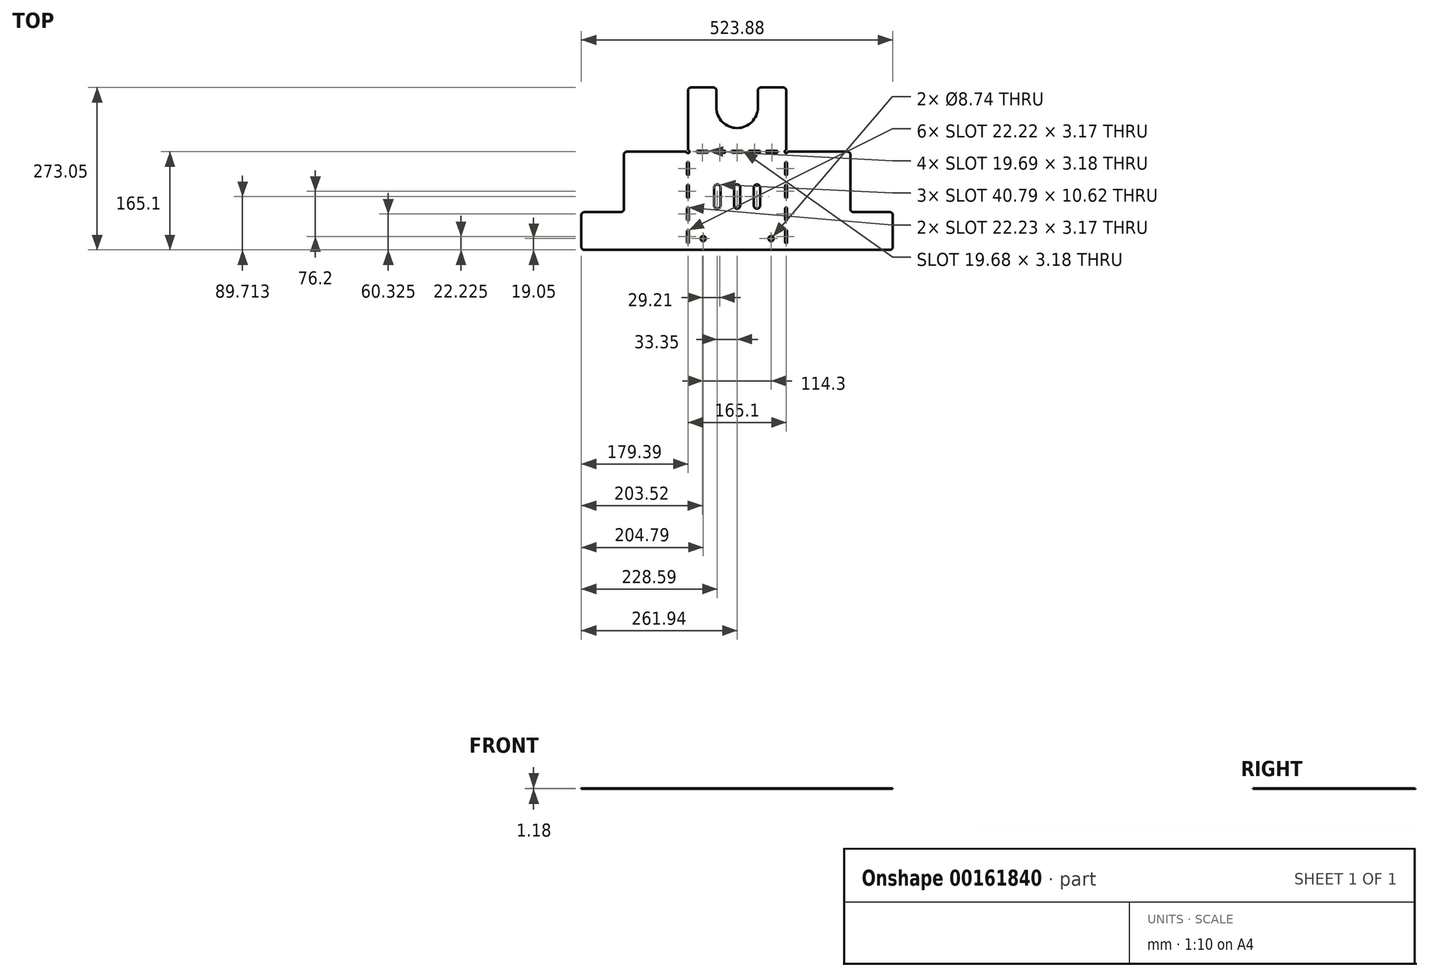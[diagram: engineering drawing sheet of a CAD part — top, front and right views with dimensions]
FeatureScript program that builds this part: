
annotation { "Feature Type Name" : "Feature", "Feature Type Description" : "" }
export const myFeature = defineFeature(function(context is Context, id is Id, definition is map)
    precondition{}
    {
        {
            var Q0;
            Q0=qCreatedBy(makeId("Top.planeOp"),FACE);
            var sketch = newSketch(context, id + "F0", { "sketchPlane" : qUnion([Q0])});
            skLineSegment(sketch, "E0", {"start": v(-82.55, 0) * mm, "end": v(82.55, 0) * mm});
            skLineSegment(sketch, "E1", {"start": v(-82.55, 0) * mm, "end": v(-82.55, 165.1) * mm});
            skLineSegment(sketch, "E2", {"start": v(82.55, 0) * mm, "end": v(82.55, 165.1) * mm});
            skLineSegment(sketch, "E3", {"start": v(-82.55, 165.1) * mm, "end": v(82.55, 165.1) * mm});
            skLineSegment(sketch, "E4", {"start": v(82.55, 0) * mm, "end": v(261.94, 0) * mm});
            skLineSegment(sketch, "E5", {"start": v(261.94, 0) * mm, "end": v(261.94, 63.5) * mm});
            skLineSegment(sketch, "E6", {"start": v(261.94, 63.5) * mm, "end": v(190.5, 63.5) * mm});
            skLineSegment(sketch, "E7", {"start": v(190.5, 63.5) * mm, "end": v(190.5, 165.1) * mm});
            skLineSegment(sketch, "E8", {"start": v(190.5, 165.1) * mm, "end": v(82.55, 165.1) * mm});
            skLineSegment(sketch, "E9", {"start": v(-82.55, 0) * mm, "end": v(-261.94, 0) * mm});
            skLineSegment(sketch, "E10", {"start": v(-261.94, 0) * mm, "end": v(-261.94, 63.5) * mm});
            skLineSegment(sketch, "E11", {"start": v(-261.94, 63.5) * mm, "end": v(-190.5, 63.5) * mm});
            skLineSegment(sketch, "E12", {"start": v(-190.5, 63.5) * mm, "end": v(-190.5, 165.1) * mm});
            skLineSegment(sketch, "E13", {"start": v(-190.5, 165.1) * mm, "end": v(-82.55, 165.1) * mm});
            skLineSegment(sketch, "E14", {"start": v(-82.55, 165.1) * mm, "end": v(-82.55, 273.05) * mm});
            skLineSegment(sketch, "E15", {"start": v(-82.55, 273.05) * mm, "end": v(-34.93, 273.05) * mm});
            skLineSegment(sketch, "E16", {"start": v(82.55, 273.05) * mm, "end": v(82.55, 165.1) * mm});
            skLineSegment(sketch, "E17", {"start": v(0, 0) * mm, "end": v(0, 365.08) * mm, "construction": true});
            skArc(sketch, "E18", {"start": v(-34.93, 239.8) * mm, "mid": v(0, 204.88) * mm, "end": v(34.93, 239.8) * mm});
            skLineSegment(sketch, "E19", {"start": v(-34.93, 239.8) * mm, "end": v(-34.93, 273.05) * mm});
            skLineSegment(sketch, "E20", {"start": v(34.93, 239.8) * mm, "end": v(34.93, 273.05) * mm});
            skLineSegment(sketch, "E21.trimOffspring", {"start": v(34.93, 273.05) * mm, "end": v(82.55, 273.05) * mm});
            skLineSegment(sketch, "E22", {"start": v(-84.14, 165.1) * mm, "end": v(-84.14, 0) * mm});
            skLineSegment(sketch, "E23", {"start": v(84.14, 165.1) * mm, "end": v(84.14, 0) * mm});
            skSolve(sketch);
        }
        {
            var Q0;
            Q0 = qSketchRegion(id + "F0", true);
            extrude(context, id + "F1", {"entities" : qUnion([Q0]), "depth" : 1.18 * mm});
        }
        {
            var Q0;
            Q0=makeQuery(id+"F1.opExtrude","CAP_FACE",FACE,{"disambiguationData":[OSD([sQuery(id+"F0.wireOp",EDGE,"E0"),sQuery(id+"F0.wireOp",EDGE,"E4"),sQuery(id+"F0.wireOp",EDGE,"E5"),sQuery(id+"F0.wireOp",EDGE,"E6"),sQuery(id+"F0.wireOp",EDGE,"E7"),sQuery(id+"F0.wireOp",EDGE,"E8"),sQuery(id+"F0.wireOp",EDGE,"E9"),sQuery(id+"F0.wireOp",EDGE,"E10"),sQuery(id+"F0.wireOp",EDGE,"E11"),sQuery(id+"F0.wireOp",EDGE,"E12"),sQuery(id+"F0.wireOp",EDGE,"E13"),sQuery(id+"F0.wireOp",EDGE,"E14"),sQuery(id+"F0.wireOp",EDGE,"E15"),sQuery(id+"F0.wireOp",EDGE,"E16"),sQuery(id+"F0.wireOp",EDGE,"E18"),sQuery(id+"F0.wireOp",EDGE,"E19"),sQuery(id+"F0.wireOp",EDGE,"E20"),sQuery(id+"F0.wireOp",EDGE,"E21.trimOffspring")])],"isStart":false});
            var sketch = newSketch(context, id + "F2", { "sketchPlane" : qUnion([Q0])});
            skLineSegment(sketch, "E24.0", {"start": v(261.94, 0) * mm, "end": v(-261.94, 0) * mm});
            skPoint(sketch, "E25.0", {"position": v(0, 0) * mm});
            skLineSegment(sketch, "E26", {"start": v(0, 74.63) * mm, "end": v(0, 104.8) * mm, "construction": true});
            skLineSegment(sketch, "E27", {"start": v(-123.7, 19.05) * mm, "end": v(130.02, 19.05) * mm, "construction": true});
            skLineSegment(sketch, "E28", {"start": v(-57.15, 51.44) * mm, "end": v(-57.15, -23.28) * mm, "construction": true});
            skLineSegment(sketch, "E29", {"start": v(57.15, 51.05) * mm, "end": v(57.15, -26) * mm, "construction": true});
            skCircle(sketch, "E30", {"center": v(-57.15, 19.05) * mm, "radius": 4.37 * mm});
            skCircle(sketch, "E31", {"center": v(57.15, 19.05) * mm, "radius": 4.37 * mm});
            skLineSegment(sketch, "E32", {"start": v(-208.63, 104.8) * mm, "end": v(250.8, 104.8) * mm, "construction": true});
            skLineSegment(sketch, "E33", {"start": v(-210.6, 74.63) * mm, "end": v(258, 74.63) * mm, "construction": true});
            skLineSegment(sketch, "E34", {"start": v(-33.35, 104.8) * mm, "end": v(-33.35, 74.63) * mm, "construction": true});
            skLineSegment(sketch, "E35", {"start": v(33.35, 104.8) * mm, "end": v(33.35, 74.63) * mm, "construction": true});
            skArc(sketch, "E36.0.startCap", {"start": v(-38.66, 104.8) * mm, "mid": v(-33.35, 110.1) * mm, "end": v(-28.04, 104.8) * mm});
            skArc(sketch, "E36.0.endCap", {"start": v(-28.04, 74.63) * mm, "mid": v(-33.35, 69.32) * mm, "end": v(-38.66, 74.63) * mm});
            skLineSegment(sketch, "E36.0.left", {"start": v(-28.04, 104.8) * mm, "end": v(-28.04, 74.63) * mm});
            skLineSegment(sketch, "E36.0.right", {"start": v(-38.66, 104.8) * mm, "end": v(-38.66, 74.63) * mm});
            skArc(sketch, "E37.0.startCap", {"start": v(5.3, 74.63) * mm, "mid": v(0, 69.32) * mm, "end": v(-5.3, 74.63) * mm});
            skArc(sketch, "E37.0.endCap", {"start": v(-5.3, 104.8) * mm, "mid": v(0, 110.1) * mm, "end": v(5.3, 104.8) * mm});
            skLineSegment(sketch, "E37.0.left", {"start": v(-5.3, 74.63) * mm, "end": v(-5.3, 104.8) * mm});
            skLineSegment(sketch, "E37.0.right", {"start": v(5.3, 74.63) * mm, "end": v(5.3, 104.8) * mm});
            skArc(sketch, "E38.0.startCap", {"start": v(28.04, 104.8) * mm, "mid": v(33.35, 110.1) * mm, "end": v(38.66, 104.8) * mm});
            skArc(sketch, "E38.0.endCap", {"start": v(38.66, 74.63) * mm, "mid": v(33.35, 69.32) * mm, "end": v(28.04, 74.63) * mm});
            skLineSegment(sketch, "E38.0.left", {"start": v(38.66, 104.8) * mm, "end": v(38.66, 74.63) * mm});
            skLineSegment(sketch, "E38.0.right", {"start": v(28.04, 104.8) * mm, "end": v(28.04, 74.63) * mm});
            skSolve(sketch);
        }
        {
            var Q0;
            Q0 = qSketchRegion(id + "F2", true);
            extrude(context, id + "F3", {"entities" : qUnion([Q0]), "operationType" : NewBodyOperationType.REMOVE, "endBound" : BoundingType.UP_TO_NEXT, "oppositeDirection" : true, "depth" : 25.4 * mm});
        }
        {
            var Q0;
            Q0=makeQuery(id+"F1.opExtrude","SWEPT_EDGE",EDGE,{"disambiguationData":[OSD([sQuery(id+"F0.wireOp",EDGE,"E14"),sQuery(id+"F0.wireOp",EDGE,"E15")])]});
            var Q1;
            Q1=makeQuery(id+"F1.opExtrude","SWEPT_EDGE",EDGE,{"disambiguationData":[OSD([sQuery(id+"F0.wireOp",EDGE,"E15"),sQuery(id+"F0.wireOp",EDGE,"E19")])]});
            var Q2;
            Q2=makeQuery(id+"F1.opExtrude","SWEPT_EDGE",EDGE,{"disambiguationData":[OSD([sQuery(id+"F0.wireOp",EDGE,"E20"),sQuery(id+"F0.wireOp",EDGE,"E21.trimOffspring")])]});
            var Q3;
            Q3=makeQuery(id+"F1.opExtrude","SWEPT_EDGE",EDGE,{"disambiguationData":[OSD([sQuery(id+"F0.wireOp",EDGE,"E16"),sQuery(id+"F0.wireOp",EDGE,"E21.trimOffspring")])]});
            var Q4;
            Q4=makeQuery(id+"F1.opExtrude","SWEPT_EDGE",EDGE,{"disambiguationData":[OSD([sQuery(id+"F0.wireOp",EDGE,"E7"),sQuery(id+"F0.wireOp",EDGE,"E8")])]});
            var Q5;
            Q5=makeQuery(id+"F1.opExtrude","SWEPT_EDGE",EDGE,{"disambiguationData":[OSD([sQuery(id+"F0.wireOp",EDGE,"E5"),sQuery(id+"F0.wireOp",EDGE,"E6")])]});
            var Q6;
            Q6=makeQuery(id+"F1.opExtrude","SWEPT_EDGE",EDGE,{"disambiguationData":[OSD([sQuery(id+"F0.wireOp",EDGE,"E6"),sQuery(id+"F0.wireOp",EDGE,"E7")])]});
            var Q7;
            Q7=makeQuery(id+"F1.opExtrude","SWEPT_EDGE",EDGE,{"disambiguationData":[OSD([sQuery(id+"F0.wireOp",EDGE,"E4"),sQuery(id+"F0.wireOp",EDGE,"E5")])]});
            var Q8;
            Q8=makeQuery(id+"F1.opExtrude","SWEPT_EDGE",EDGE,{"disambiguationData":[OSD([sQuery(id+"F0.wireOp",EDGE,"E9"),sQuery(id+"F0.wireOp",EDGE,"E10")])]});
            var Q9;
            Q9=makeQuery(id+"F1.opExtrude","SWEPT_EDGE",EDGE,{"disambiguationData":[OSD([sQuery(id+"F0.wireOp",EDGE,"E10"),sQuery(id+"F0.wireOp",EDGE,"E11")])]});
            var Q10;
            Q10=makeQuery(id+"F1.opExtrude","SWEPT_EDGE",EDGE,{"disambiguationData":[OSD([sQuery(id+"F0.wireOp",EDGE,"E11"),sQuery(id+"F0.wireOp",EDGE,"E12")])]});
            var Q11;
            Q11=makeQuery(id+"F1.opExtrude","SWEPT_EDGE",EDGE,{"disambiguationData":[OSD([sQuery(id+"F0.wireOp",EDGE,"E12"),sQuery(id+"F0.wireOp",EDGE,"E13")])]});
            fillet(context, id + "F4", {"entities" : qUnion([Q0, Q1, Q2, Q3, Q4, Q5, Q6, Q7, Q8, Q9, Q10, Q11]), "radius" : 5.08 * mm, "tangentPropagation" : true, "allowEdgeOverflow" : false});
        }
        {
            var Q0;
            Q0=makeQuery(id+"F1.opExtrude","CAP_FACE",FACE,{"disambiguationData":[OSD([sQuery(id+"F0.wireOp",EDGE,"E0"),sQuery(id+"F0.wireOp",EDGE,"E4"),sQuery(id+"F0.wireOp",EDGE,"E5"),sQuery(id+"F0.wireOp",EDGE,"E6"),sQuery(id+"F0.wireOp",EDGE,"E7"),sQuery(id+"F0.wireOp",EDGE,"E8"),sQuery(id+"F0.wireOp",EDGE,"E9"),sQuery(id+"F0.wireOp",EDGE,"E10"),sQuery(id+"F0.wireOp",EDGE,"E11"),sQuery(id+"F0.wireOp",EDGE,"E12"),sQuery(id+"F0.wireOp",EDGE,"E13"),sQuery(id+"F0.wireOp",EDGE,"E14"),sQuery(id+"F0.wireOp",EDGE,"E15"),sQuery(id+"F0.wireOp",EDGE,"E16"),sQuery(id+"F0.wireOp",EDGE,"E18"),sQuery(id+"F0.wireOp",EDGE,"E19"),sQuery(id+"F0.wireOp",EDGE,"E20"),sQuery(id+"F0.wireOp",EDGE,"E21.trimOffspring")])],"isStart":false});
            var sketch = newSketch(context, id + "F5", { "sketchPlane" : qUnion([Q0])});
            skLineSegment(sketch, "E39", {"start": v(-82.55, 146.05) * mm, "end": v(-82.55, 127) * mm});
            skLineSegment(sketch, "E40", {"start": v(0, -35.73) * mm, "end": v(0, 222.95) * mm, "construction": true});
            skPoint(sketch, "E41", {"position": v(-82.55, 146.05) * mm});
            skPoint(sketch, "E42.0.1.0", {"position": v(-82.55, 127) * mm});
            skPoint(sketch, "E42.0.2.0", {"position": v(-82.55, 107.95) * mm});
            skPoint(sketch, "E42.0.3.0", {"position": v(-82.55, 88.9) * mm});
            skPoint(sketch, "E42.0.4.0", {"position": v(-82.55, 69.85) * mm});
            skPoint(sketch, "E42.0.5.0", {"position": v(-82.55, 50.8) * mm});
            skPoint(sketch, "E42.0.6.0", {"position": v(-82.55, 31.75) * mm});
            skPoint(sketch, "E42.0.7.0", {"position": v(-82.55, 12.7) * mm});
            skLineSegment(sketch, "E42.direction1", {"start": v(-82.55, 146.05) * mm, "end": v(-57.15, 146.05) * mm, "construction": true});
            skLineSegment(sketch, "E42.direction2", {"start": v(-82.55, 146.05) * mm, "end": v(-82.55, 127) * mm, "construction": true});
            skPoint(sketch, "E43.orphan", {"position": v(-82.55, 165.1) * mm});
            skLineSegment(sketch, "E44.trimOffspring", {"start": v(-82.55, 107.95) * mm, "end": v(-82.55, 88.9) * mm});
            skPoint(sketch, "E45.orphan", {"position": v(-82.55, 0) * mm});
            skLineSegment(sketch, "E46.trimOffspring", {"start": v(-82.55, 31.75) * mm, "end": v(-82.55, 12.7) * mm});
            skLineSegment(sketch, "E47.trimOffspring", {"start": v(-82.55, 69.85) * mm, "end": v(-82.55, 50.8) * mm});
            skArc(sketch, "E48.0.startCap", {"start": v(-84.14, 146.05) * mm, "mid": v(-82.55, 147.64) * mm, "end": v(-80.96, 146.05) * mm});
            skArc(sketch, "E48.0.endCap", {"start": v(-80.96, 127) * mm, "mid": v(-82.55, 125.41) * mm, "end": v(-84.14, 127) * mm});
            skLineSegment(sketch, "E48.0.left", {"start": v(-80.96, 146.05) * mm, "end": v(-80.96, 127) * mm});
            skLineSegment(sketch, "E48.0.right", {"start": v(-84.14, 146.05) * mm, "end": v(-84.14, 127) * mm});
            skArc(sketch, "E48.1.startCap", {"start": v(-84.14, 107.95) * mm, "mid": v(-82.55, 109.54) * mm, "end": v(-80.96, 107.95) * mm});
            skArc(sketch, "E48.1.endCap", {"start": v(-80.96, 88.9) * mm, "mid": v(-82.55, 87.31) * mm, "end": v(-84.14, 88.9) * mm});
            skLineSegment(sketch, "E48.1.left", {"start": v(-80.96, 107.95) * mm, "end": v(-80.96, 88.9) * mm});
            skLineSegment(sketch, "E48.1.right", {"start": v(-84.14, 107.95) * mm, "end": v(-84.14, 88.9) * mm});
            skArc(sketch, "E48.2.startCap", {"start": v(-84.14, 69.85) * mm, "mid": v(-82.55, 71.44) * mm, "end": v(-80.96, 69.85) * mm});
            skArc(sketch, "E48.2.endCap", {"start": v(-80.96, 50.8) * mm, "mid": v(-82.55, 49.21) * mm, "end": v(-84.14, 50.8) * mm});
            skLineSegment(sketch, "E48.2.left", {"start": v(-80.96, 69.85) * mm, "end": v(-80.96, 50.8) * mm});
            skLineSegment(sketch, "E48.2.right", {"start": v(-84.14, 69.85) * mm, "end": v(-84.14, 50.8) * mm});
            skArc(sketch, "E48.3.startCap", {"start": v(-84.14, 31.75) * mm, "mid": v(-82.55, 33.34) * mm, "end": v(-80.96, 31.75) * mm});
            skArc(sketch, "E48.3.endCap", {"start": v(-80.96, 12.7) * mm, "mid": v(-82.55, 11.11) * mm, "end": v(-84.14, 12.7) * mm});
            skLineSegment(sketch, "E48.3.left", {"start": v(-80.96, 31.75) * mm, "end": v(-80.96, 12.7) * mm});
            skLineSegment(sketch, "E48.3.right", {"start": v(-84.14, 31.75) * mm, "end": v(-84.14, 12.7) * mm});
            skArc(sketch, "E49.MirrorCS", {"start": v(84.14, 146.05) * mm, "mid": v(82.55, 147.64) * mm, "end": v(80.96, 146.05) * mm});
            skArc(sketch, "E50.MirrorCS", {"start": v(80.96, 127) * mm, "mid": v(82.55, 125.41) * mm, "end": v(84.14, 127) * mm});
            skArc(sketch, "E51.MirrorCS", {"start": v(80.96, 88.9) * mm, "mid": v(82.55, 87.31) * mm, "end": v(84.14, 88.9) * mm});
            skArc(sketch, "E52.MirrorCS", {"start": v(84.14, 107.95) * mm, "mid": v(82.55, 109.54) * mm, "end": v(80.96, 107.95) * mm});
            skArc(sketch, "E53.MirrorCS", {"start": v(84.14, 69.85) * mm, "mid": v(82.55, 71.44) * mm, "end": v(80.96, 69.85) * mm});
            skArc(sketch, "E54.MirrorCS", {"start": v(80.96, 12.7) * mm, "mid": v(82.55, 11.11) * mm, "end": v(84.14, 12.7) * mm});
            skArc(sketch, "E55.MirrorCS", {"start": v(84.14, 31.75) * mm, "mid": v(82.55, 33.34) * mm, "end": v(80.96, 31.75) * mm});
            skArc(sketch, "E56.MirrorCS", {"start": v(80.96, 50.8) * mm, "mid": v(82.55, 49.21) * mm, "end": v(84.14, 50.8) * mm});
            skLineSegment(sketch, "E57.MirrorCS", {"start": v(82.55, 146.05) * mm, "end": v(82.55, 127) * mm});
            skLineSegment(sketch, "E58.MirrorCS", {"start": v(84.14, 69.85) * mm, "end": v(84.14, 50.8) * mm});
            skLineSegment(sketch, "E59.MirrorCS", {"start": v(84.14, 31.75) * mm, "end": v(84.14, 12.7) * mm});
            skLineSegment(sketch, "E60.MirrorCS", {"start": v(84.14, 146.05) * mm, "end": v(84.14, 127) * mm});
            skLineSegment(sketch, "E61.MirrorCS", {"start": v(80.96, 146.05) * mm, "end": v(80.96, 127) * mm});
            skLineSegment(sketch, "E62.MirrorCS", {"start": v(82.55, 69.85) * mm, "end": v(82.55, 50.8) * mm});
            skLineSegment(sketch, "E63.MirrorCS", {"start": v(82.55, 31.75) * mm, "end": v(82.55, 12.7) * mm});
            skLineSegment(sketch, "E64.MirrorCS", {"start": v(82.55, 107.95) * mm, "end": v(82.55, 88.9) * mm});
            skPoint(sketch, "E65.MirrorP", {"position": v(82.55, 165.1) * mm});
            skLineSegment(sketch, "E66.MirrorCS", {"start": v(82.55, 146.05) * mm, "end": v(82.55, 127) * mm, "construction": true});
            skLineSegment(sketch, "E67.MirrorCS", {"start": v(84.14, 107.95) * mm, "end": v(84.14, 88.9) * mm});
            skLineSegment(sketch, "E68.MirrorCS", {"start": v(80.96, 69.85) * mm, "end": v(80.96, 50.8) * mm});
            skLineSegment(sketch, "E69.MirrorCS", {"start": v(80.96, 31.75) * mm, "end": v(80.96, 12.7) * mm});
            skLineSegment(sketch, "E70.MirrorCS", {"start": v(80.96, 107.95) * mm, "end": v(80.96, 88.9) * mm});
            skLineSegment(sketch, "E71", {"start": v(-66.68, 165.1) * mm, "end": v(-50.17, 165.1) * mm});
            skPoint(sketch, "E72", {"position": v(-66.68, 165.1) * mm});
            skPoint(sketch, "E73", {"position": v(66.68, 165.1) * mm});
            skPoint(sketch, "E74", {"position": v(-37.47, 165.1) * mm});
            skPoint(sketch, "E75", {"position": v(0, 165.1) * mm});
            skPoint(sketch, "E76", {"position": v(37.47, 165.1) * mm});
            skPoint(sketch, "E77", {"position": v(-20.96, 165.1) * mm});
            skPoint(sketch, "E78", {"position": v(20.96, 165.1) * mm});
            skPoint(sketch, "E79", {"position": v(-8.26, 165.1) * mm});
            skPoint(sketch, "E80", {"position": v(8.26, 165.1) * mm});
            skLineSegment(sketch, "E81.trimOffspring", {"start": v(-8.26, 165.1) * mm, "end": v(8.26, 165.1) * mm});
            skLineSegment(sketch, "E82.trimOffspring", {"start": v(20.96, 165.1) * mm, "end": v(37.47, 165.1) * mm});
            skPoint(sketch, "E83", {"position": v(50.17, 165.1) * mm});
            skPoint(sketch, "E84", {"position": v(-50.17, 165.1) * mm});
            skLineSegment(sketch, "E85.trimOffspring", {"start": v(-37.47, 165.1) * mm, "end": v(-20.96, 165.1) * mm});
            skLineSegment(sketch, "E86.trimOffspring", {"start": v(50.17, 165.1) * mm, "end": v(66.68, 165.1) * mm});
            skArc(sketch, "E87.0.startCap", {"start": v(-66.68, 163.51) * mm, "mid": v(-68.26, 165.1) * mm, "end": v(-66.68, 166.69) * mm});
            skArc(sketch, "E87.0.endCap", {"start": v(-50.17, 166.69) * mm, "mid": v(-48.58, 165.1) * mm, "end": v(-50.17, 163.51) * mm});
            skLineSegment(sketch, "E87.0.left", {"start": v(-66.68, 166.69) * mm, "end": v(-50.17, 166.69) * mm});
            skLineSegment(sketch, "E87.0.right", {"start": v(-66.68, 163.51) * mm, "end": v(-50.17, 163.51) * mm});
            skArc(sketch, "E87.1.startCap", {"start": v(-37.47, 163.51) * mm, "mid": v(-39.05, 165.1) * mm, "end": v(-37.47, 166.69) * mm});
            skArc(sketch, "E87.1.endCap", {"start": v(-20.96, 166.69) * mm, "mid": v(-19.37, 165.1) * mm, "end": v(-20.96, 163.51) * mm});
            skLineSegment(sketch, "E87.1.left", {"start": v(-37.47, 166.69) * mm, "end": v(-20.96, 166.69) * mm});
            skLineSegment(sketch, "E87.1.right", {"start": v(-37.47, 163.51) * mm, "end": v(-20.96, 163.51) * mm});
            skArc(sketch, "E87.2.startCap", {"start": v(-8.26, 163.51) * mm, "mid": v(-9.84, 165.1) * mm, "end": v(-8.26, 166.69) * mm});
            skArc(sketch, "E87.2.endCap", {"start": v(8.26, 166.69) * mm, "mid": v(9.84, 165.1) * mm, "end": v(8.26, 163.51) * mm});
            skLineSegment(sketch, "E87.2.left", {"start": v(-8.26, 166.69) * mm, "end": v(8.26, 166.69) * mm});
            skLineSegment(sketch, "E87.2.right", {"start": v(-8.25, 163.51) * mm, "end": v(8.26, 163.51) * mm});
            skArc(sketch, "E87.3.startCap", {"start": v(20.96, 163.51) * mm, "mid": v(19.37, 165.1) * mm, "end": v(20.96, 166.69) * mm});
            skArc(sketch, "E87.3.endCap", {"start": v(37.47, 166.69) * mm, "mid": v(39.05, 165.1) * mm, "end": v(37.47, 163.51) * mm});
            skLineSegment(sketch, "E87.3.left", {"start": v(20.96, 166.69) * mm, "end": v(37.47, 166.69) * mm});
            skLineSegment(sketch, "E87.3.right", {"start": v(20.96, 163.51) * mm, "end": v(37.47, 163.51) * mm});
            skArc(sketch, "E87.4.startCap", {"start": v(50.17, 163.51) * mm, "mid": v(48.58, 165.1) * mm, "end": v(50.17, 166.69) * mm});
            skArc(sketch, "E87.4.endCap", {"start": v(66.68, 166.69) * mm, "mid": v(68.26, 165.1) * mm, "end": v(66.68, 163.51) * mm});
            skLineSegment(sketch, "E87.4.left", {"start": v(50.17, 166.69) * mm, "end": v(66.68, 166.69) * mm});
            skLineSegment(sketch, "E87.4.right", {"start": v(50.17, 163.51) * mm, "end": v(66.68, 163.51) * mm});
            skCircle(sketch, "E88", {"center": v(-82.55, 165.1) * mm, "radius": 2.54 * mm});
            skCircle(sketch, "E89", {"center": v(82.55, 165.1) * mm, "radius": 2.54 * mm});
            skSolve(sketch);
        }
        {
            var Q0;
            Q0 = qSketchRegion(id + "F5", true);
            extrude(context, id + "F6", {"entities" : qUnion([Q0]), "operationType" : NewBodyOperationType.REMOVE, "endBound" : BoundingType.UP_TO_NEXT, "oppositeDirection" : true, "depth" : 25.4 * mm});
        }
    });
